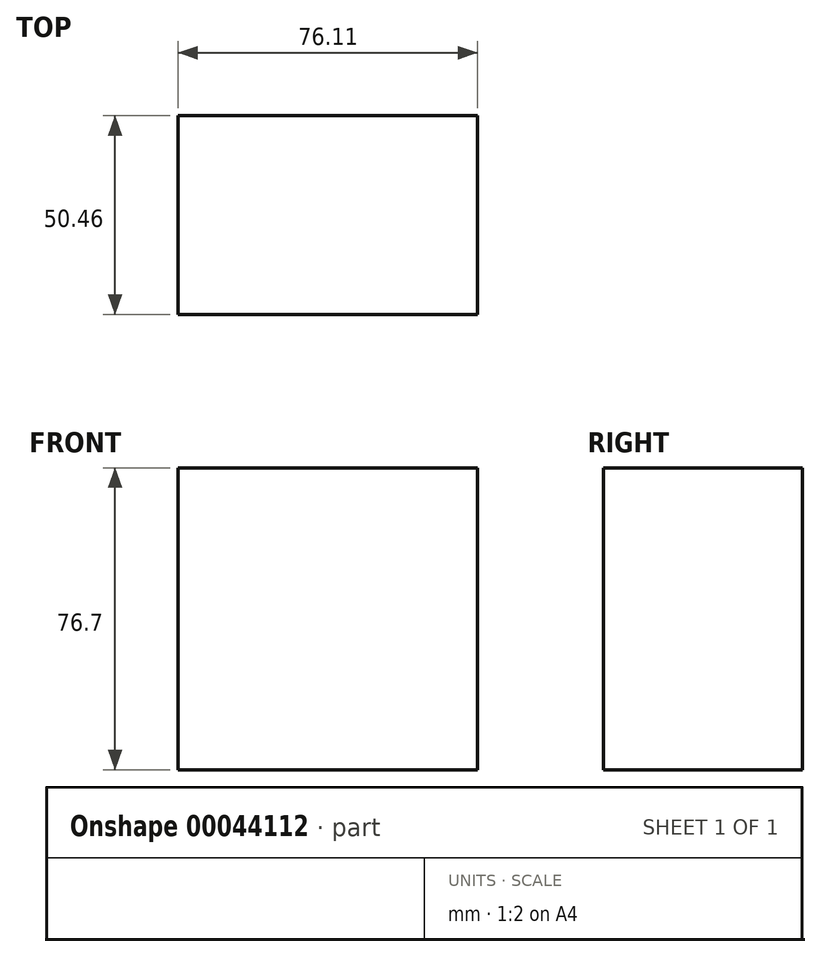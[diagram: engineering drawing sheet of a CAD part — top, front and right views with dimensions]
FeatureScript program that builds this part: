
annotation { "Feature Type Name" : "Feature", "Feature Type Description" : "" }
export const myFeature = defineFeature(function(context is Context, id is Id, definition is map)
    precondition{}
    {
        {
            var Q0;
            Q0=qCreatedBy(makeId("Front.planeOp"),FACE);
            var sketch = newSketch(context, id + "F0", { "sketchPlane" : qUnion([Q0])});
            skLineSegment(sketch, "E0", {"start": v(0, 0) * mm, "end": v(76.11, 0) * mm});
            skLineSegment(sketch, "E1", {"start": v(76.11, 0) * mm, "end": v(76.11, 76.7) * mm});
            skLineSegment(sketch, "E2", {"start": v(76.11, 76.7) * mm, "end": v(0, 76.7) * mm});
            skLineSegment(sketch, "E3", {"start": v(0, 76.7) * mm, "end": v(0, 0) * mm});
            skSolve(sketch);
        }
        {
            var Q0;
            Q0=makeQuery(id+"F0.imprint","IMPRINT",FACE,{"disambiguationData":[TD([[makeQuery(id+"F0.imprint","IMPRINT",EDGE,{"derivedFrom":sQuery(id+"F0.wireOp",EDGE,"E0")}),1.0]])]});
            extrude(context, id + "F1", {"entities" : qUnion([Q0]), "depth" : 80.45 * mm, "hasSecondDirection" : true, "secondDirectionOppositeDirection" : false, "secondDirectionDepth" : 29.99 * mm});
        }
    });
